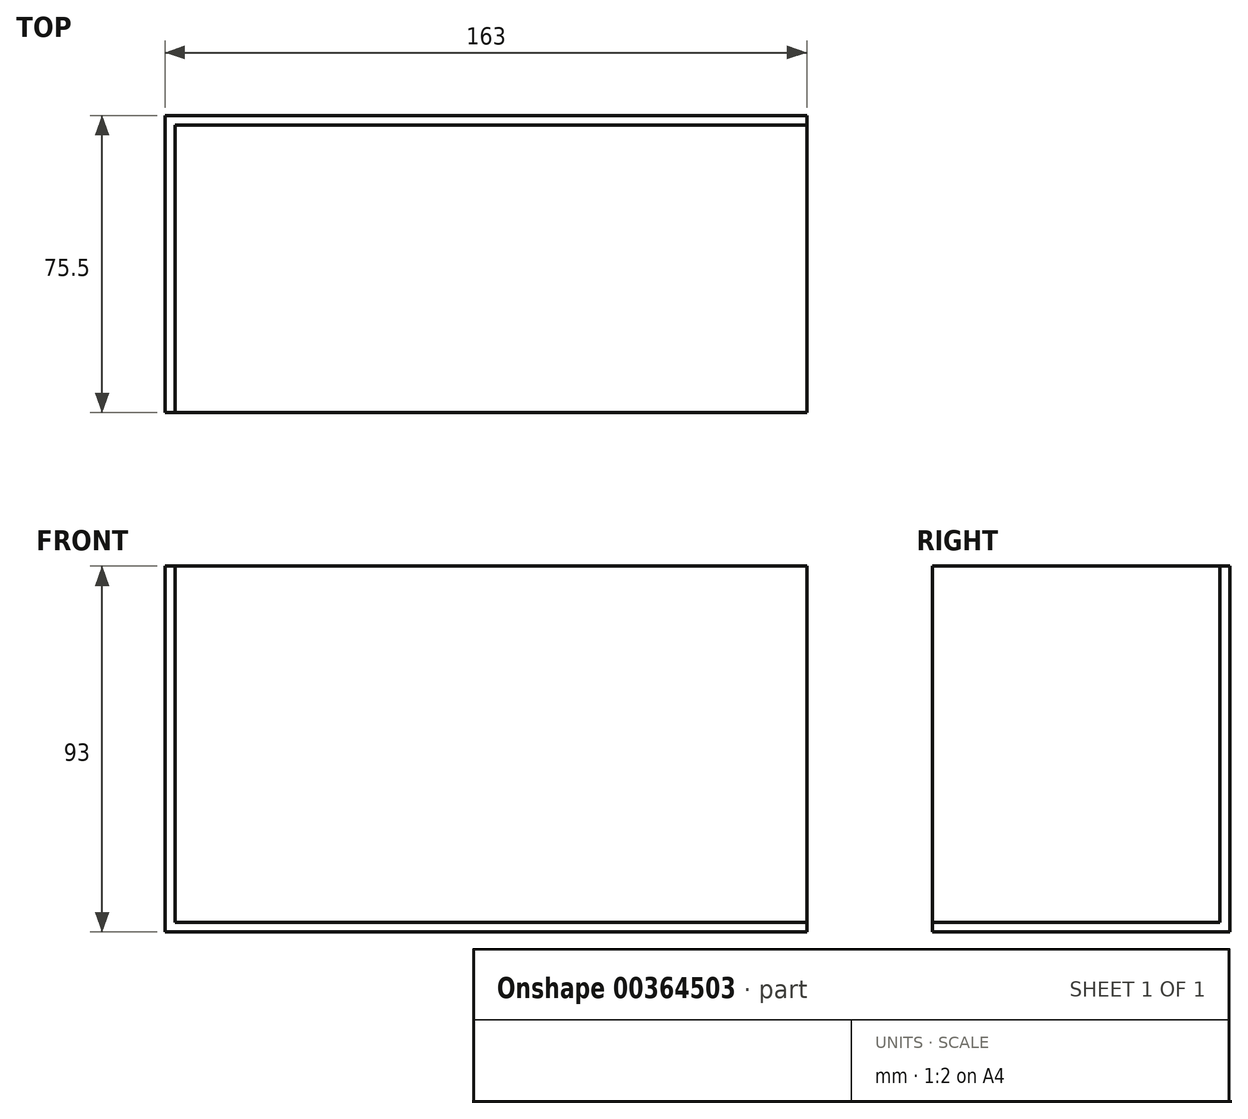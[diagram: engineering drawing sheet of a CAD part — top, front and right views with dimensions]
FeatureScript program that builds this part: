
annotation { "Feature Type Name" : "Feature", "Feature Type Description" : "" }
export const myFeature = defineFeature(function(context is Context, id is Id, definition is map)
    precondition{}
    {
        {
            var Q0;
            Q0=qCreatedBy(makeId("Right.planeOp"),FACE);
            var sketch = newSketch(context, id + "F0", { "sketchPlane" : qUnion([Q0])});
            skLineSegment(sketch, "E0.bottom", {"start": v(-158.9, 20.06) * mm, "end": v(-80.9, 20.06) * mm});
            skLineSegment(sketch, "E0.top", {"start": v(-158.9, -72.94) * mm, "end": v(-80.9, -72.94) * mm});
            skLineSegment(sketch, "E0.left", {"start": v(-158.9, 20.06) * mm, "end": v(-158.9, -72.94) * mm});
            skLineSegment(sketch, "E0.right", {"start": v(-80.9, 20.06) * mm, "end": v(-80.9, -72.94) * mm});
            skSolve(sketch);
        }
        {
            var Q0;
            Q0=makeQuery(id+"F0.imprint","IMPRINT",FACE,{"disambiguationData":[TD([[makeQuery(id+"F0.imprint","IMPRINT",EDGE,{"derivedFrom":sQuery(id+"F0.wireOp",EDGE,"E0.bottom")}),-1.0]])]});
            extrude(context, id + "F1", {"entities" : qUnion([Q0]), "depth" : 163 * mm});
        }
        {
            var Q0;
            Q0=makeQuery(id+"F1.opExtrude","SWEPT_FACE",FACE,{"disambiguationData":[OSD([sQuery(id+"F0.wireOp",EDGE,"E0.bottom")])]});
            shell(context, id + "F2", {"entities" : qUnion([Q0]), "thickness" : 2.5 * mm});
        }
        {
            var Q0;
            Q0=makeQuery(id+"F1.opExtrude","SWEPT_FACE",FACE,{"disambiguationData":[OSD([sQuery(id+"F0.wireOp",EDGE,"E0.left")])]});
            extrude(context, id + "F3", {"entities" : qUnion([Q0]), "operationType" : NewBodyOperationType.ADD, "oppositeDirection" : true, "depth" : 2.5 * mm});
        }
        {
            var Q0;
            Q0=makeQuery(id+"F1.opExtrude","SWEPT_FACE",FACE,{"disambiguationData":[OSD([sQuery(id+"F0.wireOp",EDGE,"E0.left")])]});
            extrude(context, id + "F4", {"entities" : qUnion([Q0]), "operationType" : NewBodyOperationType.REMOVE, "oppositeDirection" : true, "depth" : 2.5 * mm});
        }
        {
            var Q0;
            {var subQ0=sQuery(id+"F0.wireOp",EDGE,"E0.right");var subQ1=sQuery(id+"F0.wireOp",EDGE,"E0.left");var subQ2=sQuery(id+"F0.wireOp",EDGE,"E0.top");var subQ3=sQuery(id+"F0.wireOp",EDGE,"E0.bottom");Q0=makeQuery(id+"F2.opShell","OFFSET_FACE",FACE,{"disambiguationData":[OSD([subQ3,subQ2,subQ1,subQ0]),TDD([makeQuery(id+"F1.opExtrude","CAP_FACE",FACE,{"disambiguationData":[OSD([subQ3,subQ2,subQ1,subQ0])],"isStart":false})])]});}
            extrude(context, id + "F5", {"entities" : qUnion([Q0]), "operationType" : NewBodyOperationType.REMOVE, "oppositeDirection" : true, "depth" : 25 * mm});
        }
    });
